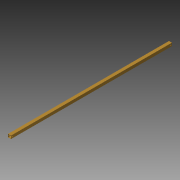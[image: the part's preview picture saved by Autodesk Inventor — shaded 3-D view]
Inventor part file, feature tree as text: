
AUTODESK INVENTOR PART (.ipt)
format: ipt  version: 2015 (Build 190159000, 159)  size: 92,160 bytes
history: native  units: in
note: dims shown in document units (in); Inventor stores cm internally (conversion verified against a paired STEP export)
features: extrude x2, sketch x2, projected_geometry x1
ambient origin geometry x8: Origin, YZ Plane, XZ Plane, XY Plane, X Axis, Y Axis, Z Axis, Center Point
bodies: Solid1 (feature_tree)
feature tree (5):
  extrude  "Extrusion1"  Depth=0.05in
  extrude  "Extrusion2"  TaperAngle=0.0deg  [1 undecoded]
  sketch  "Sketch1"  dims[d0=1.0in d1=0.05in]
  sketch  "Sketch2"  dims[d2=54.5in d3=0.0in d4=0.375in d5=0.375in d6=0.5in d7=54.5in d8=0.0in]
  projected_geometry  "Projected Loop1"
note: 1 required parameter value undecoded (feature->parameter linkage not recoverable at this tier; creation-order binding heuristic only, values carry confidence <= 0.55)
